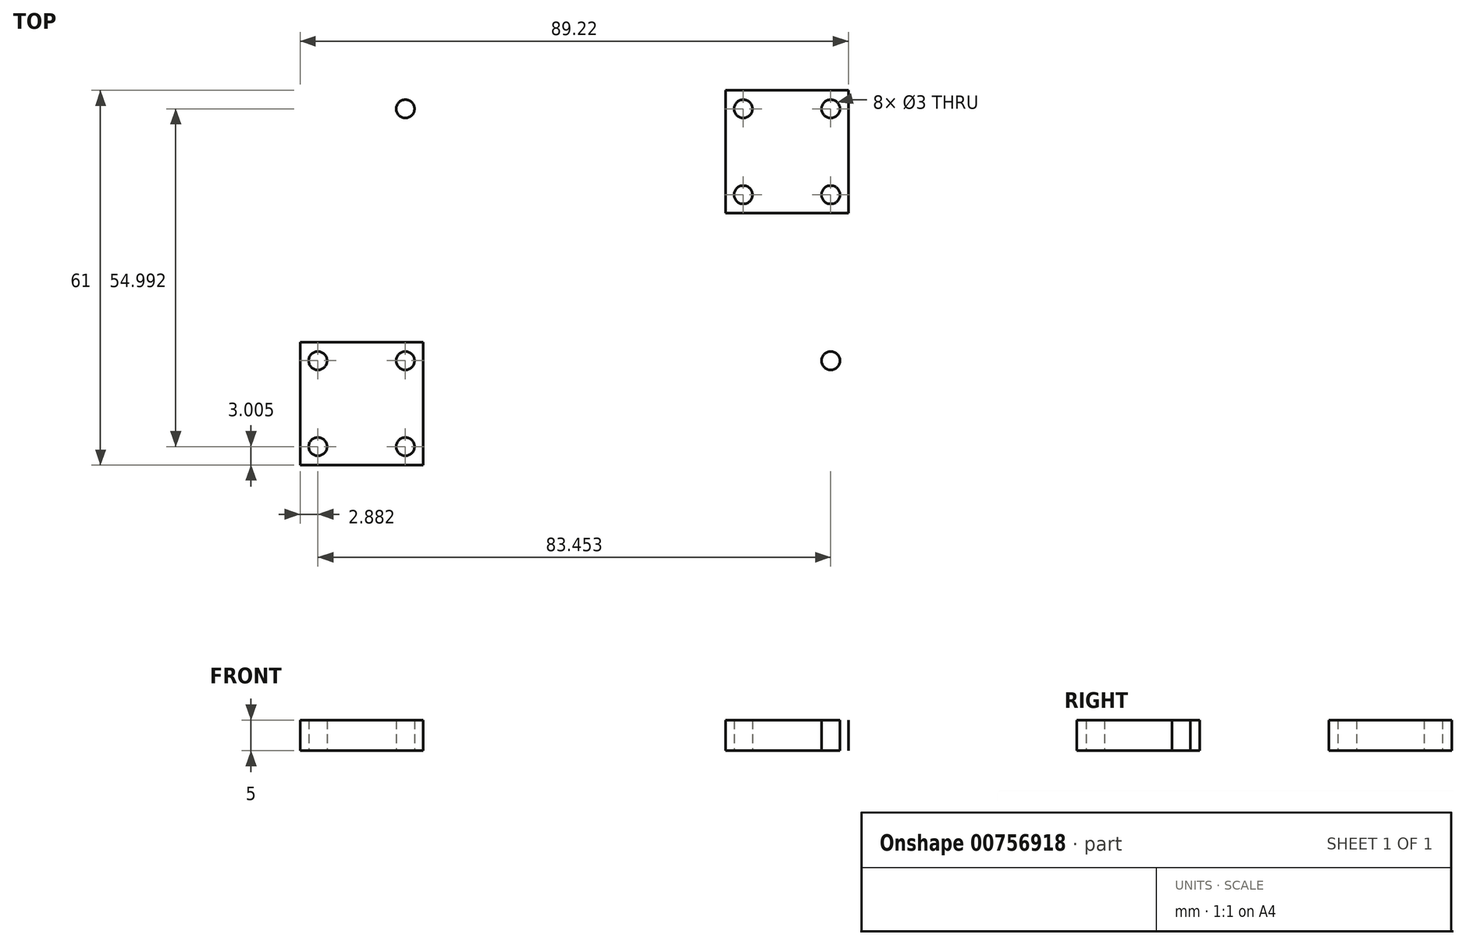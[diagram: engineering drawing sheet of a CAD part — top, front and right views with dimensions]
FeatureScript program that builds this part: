
annotation { "Feature Type Name" : "Feature", "Feature Type Description" : "" }
export const myFeature = defineFeature(function(context is Context, id is Id, definition is map)
    precondition{}
    {
        {
            var Q0;
            Q0=qCreatedBy(makeId("Top.planeOp"),FACE);
            var sketch = newSketch(context, id + "F0", { "sketchPlane" : qUnion([Q0])});
            skLineSegment(sketch, "E0.MirrorCS", {"start": v(-10, 31) * mm, "end": v(10, 31) * mm});
            skLineSegment(sketch, "E1.MirrorCS", {"start": v(-10, 31) * mm, "end": v(-10, 51) * mm});
            skLineSegment(sketch, "E2.MirrorCS", {"start": v(10, 31) * mm, "end": v(10, 51) * mm});
            skLineSegment(sketch, "E3.MirrorCS", {"start": v(-10, 51) * mm, "end": v(10, 51) * mm});
            skCircle(sketch, "E4", {"center": v(-7.12, 48) * mm, "radius": 1.5 * mm});
            skCircle(sketch, "E5.MirrorC", {"center": v(7.12, 48) * mm, "radius": 1.5 * mm});
            skCircle(sketch, "E6.MirrorC", {"center": v(-7.12, 34) * mm, "radius": 1.5 * mm});
            skCircle(sketch, "E7.MirrorC", {"center": v(7.12, 34) * mm, "radius": 1.5 * mm});
            skCircle(sketch, "E8.MirrorC", {"center": v(7.12, 7) * mm, "radius": 1.5 * mm});
            skCircle(sketch, "E9.MirrorC", {"center": v(-7.12, 7) * mm, "radius": 1.5 * mm});
            skCircle(sketch, "E10.MirrorC", {"center": v(7.12, -7) * mm, "radius": 1.5 * mm});
            skCircle(sketch, "E11.MirrorC", {"center": v(-7.12, -7) * mm, "radius": 1.5 * mm});
            skLineSegment(sketch, "E12.MirrorCS", {"start": v(10, 10) * mm, "end": v(10, -10) * mm});
            skLineSegment(sketch, "E13.MirrorCS", {"start": v(-10, 10) * mm, "end": v(10, 10) * mm});
            skLineSegment(sketch, "E14.MirrorCS", {"start": v(-10, -10) * mm, "end": v(10, -10) * mm});
            skLineSegment(sketch, "E15.MirrorCS", {"start": v(-10, 10) * mm, "end": v(-10, -10) * mm});
            skLineSegment(sketch, "E16", {"start": v(-34.61, 61.26) * mm, "end": v(-34.61, -40.28) * mm});
            skCircle(sketch, "E17.MirrorC", {"center": v(-62.1, 48) * mm, "radius": 1.5 * mm});
            skCircle(sketch, "E18.MirrorC", {"center": v(-76.34, 48) * mm, "radius": 1.5 * mm});
            skCircle(sketch, "E19.MirrorC", {"center": v(-62.1, 34) * mm, "radius": 1.5 * mm});
            skCircle(sketch, "E20.MirrorC", {"center": v(-76.34, 34) * mm, "radius": 1.5 * mm});
            skCircle(sketch, "E21.MirrorC", {"center": v(-76.34, 7) * mm, "radius": 1.5 * mm});
            skCircle(sketch, "E22.MirrorC", {"center": v(-62.1, 7) * mm, "radius": 1.5 * mm});
            skCircle(sketch, "E23.MirrorC", {"center": v(-76.34, -7) * mm, "radius": 1.5 * mm});
            skCircle(sketch, "E24.MirrorC", {"center": v(-62.1, -7) * mm, "radius": 1.5 * mm});
            skLineSegment(sketch, "E25.MirrorCS", {"start": v(-59.22, 10) * mm, "end": v(-79.22, 10) * mm});
            skLineSegment(sketch, "E26.MirrorCS", {"start": v(-59.22, -10) * mm, "end": v(-79.22, -10) * mm});
            skLineSegment(sketch, "E27.MirrorCS", {"start": v(-59.22, 10) * mm, "end": v(-59.22, -10) * mm});
            skLineSegment(sketch, "E28.MirrorCS", {"start": v(-59.22, 31) * mm, "end": v(-79.22, 31) * mm});
            skLineSegment(sketch, "E29.MirrorCS", {"start": v(-59.22, 31) * mm, "end": v(-59.22, 51) * mm});
            skLineSegment(sketch, "E30.MirrorCS", {"start": v(-79.22, 31) * mm, "end": v(-79.22, 51) * mm});
            skLineSegment(sketch, "E31.MirrorCS", {"start": v(-59.22, 51) * mm, "end": v(-79.22, 51) * mm});
            skLineSegment(sketch, "E32.MirrorCS", {"start": v(-79.22, 10) * mm, "end": v(-79.22, -10) * mm});
            skSolve(sketch);
        }
        {
            var Q0;
            Q0=makeQuery(id+"F0.imprint","IMPRINT",FACE,{"disambiguationData":[TD([[makeQuery(id+"F0.imprint","IMPRINT",EDGE,{"derivedFrom":sQuery(id+"F0.wireOp",EDGE,"E0.MirrorCS")}),1.0]])]});
            extrude(context, id + "F1", {"entities" : qUnion([Q0]), "depth" : 5 * mm, "offsetDistance" : 25 * mm});
        }
        {
            var Q0;
            Q0=makeQuery(id+"F0.imprint","IMPRINT",FACE,{"disambiguationData":[TD([[makeQuery(id+"F0.imprint","IMPRINT",EDGE,{"derivedFrom":sQuery(id+"F0.wireOp",EDGE,"E8.MirrorC")}),1.0]])]});
            extrude(context, id + "F2", {"entities" : qUnion([Q0]), "depth" : 5 * mm, "offsetDistance" : 25 * mm});
        }
        {
            var Q0;
            Q0=makeQuery(id+"F0.imprint","IMPRINT",FACE,{"disambiguationData":[TD([[makeQuery(id+"F0.imprint","IMPRINT",EDGE,{"derivedFrom":sQuery(id+"F0.wireOp",EDGE,"E17.MirrorC")}),1.0]])]});
            var Q1;
            Q1=makeQuery(id+"F0.imprint","IMPRINT",FACE,{"disambiguationData":[TD([[makeQuery(id+"F0.imprint","IMPRINT",EDGE,{"derivedFrom":sQuery(id+"F0.wireOp",EDGE,"E21.MirrorC")}),-1.0]])]});
            extrude(context, id + "F3", {"entities" : qUnion([Q0, Q1]), "depth" : 5 * mm, "offsetDistance" : 25 * mm});
        }
    });
